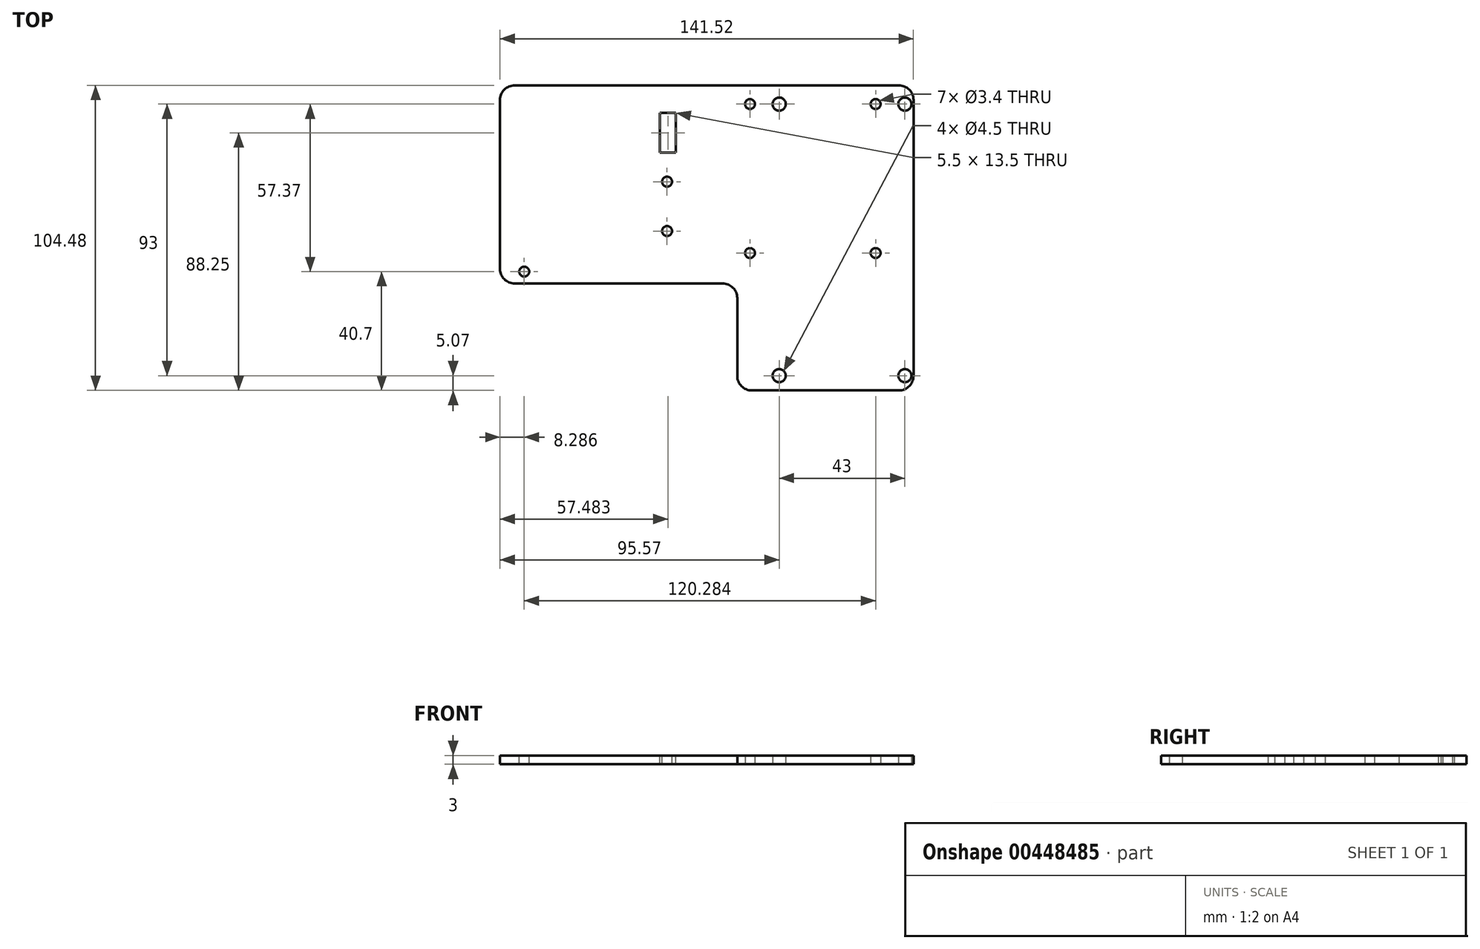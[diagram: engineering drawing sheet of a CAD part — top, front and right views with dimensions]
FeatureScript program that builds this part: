
annotation { "Feature Type Name" : "Feature", "Feature Type Description" : "" }
export const myFeature = defineFeature(function(context is Context, id is Id, definition is map)
    precondition{}
    {
        {
            var Q0;
            Q0=qCreatedBy(makeId("Top.planeOp"),FACE);
            var sketch = newSketch(context, id + "F0", { "sketchPlane" : qUnion([Q0])});
            skLineSegment(sketch, "E0.bottom", {"start": v(-21.5, 46.5) * mm, "end": v(21.5, 46.5) * mm, "construction": true});
            skLineSegment(sketch, "E0.top", {"start": v(-21.5, -46.5) * mm, "end": v(21.5, -46.5) * mm, "construction": true});
            skLineSegment(sketch, "E0.left", {"start": v(-21.5, 46.5) * mm, "end": v(-21.5, -46.5) * mm, "construction": true});
            skLineSegment(sketch, "E0.right", {"start": v(21.5, 46.5) * mm, "end": v(21.5, -46.5) * mm, "construction": true});
            skPoint(sketch, "E0.middle", {"position": v(0, 0) * mm});
            skLineSegment(sketch, "E1.bottom", {"start": v(24.45, -51.57) * mm, "end": v(-35.85, -51.57) * mm});
            skLineSegment(sketch, "E1.top", {"start": v(24.45, 52.91) * mm, "end": v(-117.07, 52.91) * mm});
            skLineSegment(sketch, "E1.left", {"start": v(24.45, -51.57) * mm, "end": v(24.45, 52.91) * mm});
            skLineSegment(sketch, "E1.right", {"start": v(-117.07, -14.94) * mm, "end": v(-117.07, 52.91) * mm});
            skPoint(sketch, "E2.orphan", {"position": v(-96.4, 75.9) * mm});
            skLineSegment(sketch, "E3.0", {"start": v(11.5, 46.5) * mm, "end": v(11.5, -4.5) * mm});
            skLineSegment(sketch, "E4.0", {"start": v(-31.5, 46.5) * mm, "end": v(-31.5, -4.5) * mm});
            skLineSegment(sketch, "E5", {"start": v(-117.07, -14.94) * mm, "end": v(-35.85, -14.94) * mm});
            skLineSegment(sketch, "E6", {"start": v(-35.85, -14.94) * mm, "end": v(-35.85, -51.57) * mm});
            skSolve(sketch);
        }
        {
            var Q0;
            Q0 = qSketchRegion(id + "F0", true);
            extrude(context, id + "F1", {"entities" : qUnion([Q0]), "depth" : 3 * mm, "offsetDistance" : 25 * mm});
        }
        {
            var Q0;
            Q0=sQuery(id+"F0.wireOp",VERTEX,"E0.left.start");
            var Q1;
            Q1=sQuery(id+"F0.wireOp",VERTEX,"E0.right.start");
            var Q2;
            Q2=sQuery(id+"F0.wireOp",VERTEX,"E0.right.end");
            var Q3;
            Q3=sQuery(id+"F0.wireOp",VERTEX,"E0.left.end");
            var Q4;
            Q4=makeQuery(id+"F1.opExtrude","SWEPT_BODY",BODY,{"disambiguationData":[OSD([sQuery(id+"F0.wireOp",EDGE,"E1.bottom"),sQuery(id+"F0.wireOp",EDGE,"E1.top"),sQuery(id+"F0.wireOp",EDGE,"E1.left"),sQuery(id+"F0.wireOp",EDGE,"E1.right"),sQuery(id+"F0.wireOp",EDGE,"YAgUvNzY-ITle-nGsT-Vmnw-g5ldA8nWUGnr"),sQuery(id+"F0.wireOp",EDGE,"XyIVaQW3-El7N-e6bz-1eAk-mJc9jGYG2OAW"),sQuery(id+"F0.wireOp",EDGE,"2inYUX5w-coaZ-2hAe-3aFK-Vs1NiTnumc5f"),sQuery(id+"F0.wireOp",EDGE,"RIFZKn75-bQRI-PPT5-OLLJ-XKhDclTj2aRo")])]});
            hole(context, id + "F2", {"style" : HoleStyle.SIMPLE, "endStyle" : HoleEndStyle.THROUGH, "oppositeDirection" : true, "holeDiameter" : 4.5 * mm, "majorDiameter" : 5 * mm, "isTappedThrough" : true, "tappedDepth" : 12 * mm, "tapClearance" : 3, "startFromSketch" : true, "locations" : qUnion([Q0, Q1, Q2, Q3]), "scope" : qUnion([Q4])});
        }
        {
            var Q0;
            Q0=makeQuery(id+"F1.opExtrude","SWEPT_EDGE",EDGE,{"disambiguationData":[OSD([sQuery(id+"F0.wireOp",EDGE,"E1.top"),sQuery(id+"F0.wireOp",EDGE,"E1.right")])]});
            var Q1;
            Q1=makeQuery(id+"F1.opExtrude","SWEPT_EDGE",EDGE,{"disambiguationData":[OSD([sQuery(id+"F0.wireOp",EDGE,"XyIVaQW3-El7N-e6bz-1eAk-mJc9jGYG2OAW"),sQuery(id+"F0.wireOp",EDGE,"2inYUX5w-coaZ-2hAe-3aFK-Vs1NiTnumc5f")])]});
            var Q2;
            Q2=makeQuery(id+"F1.opExtrude","SWEPT_EDGE",EDGE,{"disambiguationData":[OSD([sQuery(id+"F0.wireOp",EDGE,"YAgUvNzY-ITle-nGsT-Vmnw-g5ldA8nWUGnr"),sQuery(id+"F0.wireOp",EDGE,"XyIVaQW3-El7N-e6bz-1eAk-mJc9jGYG2OAW")])]});
            var Q3;
            Q3=makeQuery(id+"F1.opExtrude","SWEPT_EDGE",EDGE,{"disambiguationData":[OSD([sQuery(id+"F0.wireOp",EDGE,"YAgUvNzY-ITle-nGsT-Vmnw-g5ldA8nWUGnr"),sQuery(id+"F0.wireOp",EDGE,"RIFZKn75-bQRI-PPT5-OLLJ-XKhDclTj2aRo")])]});
            var Q4;
            Q4=makeQuery(id+"F1.opExtrude","SWEPT_EDGE",EDGE,{"disambiguationData":[OSD([sQuery(id+"F0.wireOp",EDGE,"E1.bottom"),sQuery(id+"F0.wireOp",EDGE,"2inYUX5w-coaZ-2hAe-3aFK-Vs1NiTnumc5f")])]});
            var Q5;
            Q5=makeQuery(id+"F1.opExtrude","SWEPT_EDGE",EDGE,{"disambiguationData":[OSD([sQuery(id+"F0.wireOp",EDGE,"E1.right"),sQuery(id+"F0.wireOp",EDGE,"RIFZKn75-bQRI-PPT5-OLLJ-XKhDclTj2aRo")])]});
            var Q6;
            Q6=makeQuery(id+"F1.opExtrude","SWEPT_EDGE",EDGE,{"disambiguationData":[OSD([sQuery(id+"F0.wireOp",EDGE,"E1.top"),sQuery(id+"F0.wireOp",EDGE,"E1.left")])]});
            var Q7;
            Q7=makeQuery(id+"F1.opExtrude","SWEPT_EDGE",EDGE,{"disambiguationData":[OSD([sQuery(id+"F0.wireOp",EDGE,"E1.bottom"),sQuery(id+"F0.wireOp",EDGE,"E1.left")])]});
            var Q8;
            Q8=makeQuery(id+"F1.opExtrude","SWEPT_EDGE",EDGE,{"disambiguationData":[OSD([sQuery(id+"F0.wireOp",EDGE,"Mbf7E7DW-qALH-cvkv-Damv-hvnqM2JEZsVI"),sQuery(id+"F0.wireOp",EDGE,"yL2UZmJc-QStA-b8Vo-1v86-bxjpKFNwprbL")])]});
            var Q9;
            Q9=makeQuery(id+"F1.opExtrude","SWEPT_EDGE",EDGE,{"disambiguationData":[OSD([sQuery(id+"F0.wireOp",EDGE,"qiIUHCKB-fCWY-SWhl-cjjz-M1Dty9vsqyQJ"),sQuery(id+"F0.wireOp",EDGE,"Q55u8Cbf-FWXE-ZP9w-DCtp-IPOpDFhRQxLW")])]});
            var Q10;
            Q10=makeQuery(id+"F1.opExtrude","SWEPT_EDGE",EDGE,{"disambiguationData":[OSD([sQuery(id+"F0.wireOp",EDGE,"a1f7CNFQ-nP29-92E3-ja6P-g6eo9MA6HpaG"),sQuery(id+"F0.wireOp",EDGE,"OeeX4dYa-ce1g-dk9C-RiQx-GZsGsBV5ChxM")])]});
            var Q11;
            Q11=makeQuery(id+"F1.opExtrude","SWEPT_EDGE",EDGE,{"disambiguationData":[OSD([sQuery(id+"F0.wireOp",EDGE,"OeeX4dYa-ce1g-dk9C-RiQx-GZsGsBV5ChxM"),sQuery(id+"F0.wireOp",EDGE,"j85sN3cy-DIR5-E17b-kCIM-lPXGn6SRW4FC")])]});
            var Q12;
            Q12=makeQuery(id+"F1.opExtrude","SWEPT_EDGE",EDGE,{"disambiguationData":[OSD([sQuery(id+"F0.wireOp",EDGE,"H5cnSjnK-4Nrg-yr1O-NTxU-GIKtI7yp09dG"),sQuery(id+"F0.wireOp",EDGE,"aUoxsp5O-AR9o-Et6y-4KpD-5wgRAlL37lOh")])]});
            var Q13;
            Q13=makeQuery(id+"F1.opExtrude","SWEPT_EDGE",EDGE,{"disambiguationData":[OSD([sQuery(id+"F0.wireOp",EDGE,"9UlV4Nop-iNJr-02NP-fapv-DWM8Iypxcy4n"),sQuery(id+"F0.wireOp",EDGE,"RAkMmiOb-nROR-mXBJ-D0fB-59uvw5uzIgUD")])]});
            var Q14;
            Q14=makeQuery(id+"F1.opExtrude","SWEPT_EDGE",EDGE,{"disambiguationData":[OSD([sQuery(id+"F0.wireOp",EDGE,"RpWV4TA2-qZx3-hfFS-Fjk5-bPTjN17klhtH"),sQuery(id+"F0.wireOp",EDGE,"2l11ivdO-LSoy-1MMf-z1oK-tAifx8Baqm9W")])]});
            var Q15;
            Q15=makeQuery(id+"F1.opExtrude","SWEPT_EDGE",EDGE,{"disambiguationData":[OSD([sQuery(id+"F0.wireOp",EDGE,"E5"),sQuery(id+"F0.wireOp",EDGE,"E6")])]});
            fillet(context, id + "F3", {"entities" : qUnion([Q0, Q1, Q2, Q3, Q4, Q5, Q6, Q7, Q8, Q9, Q10, Q11, Q12, Q13, Q14, Q15]), "radius" : 5 * mm, "tangentPropagation" : true, "allowEdgeOverflow" : false});
        }
        {
            var Q0;
            Q0=sQuery(id+"F0.wireOp",VERTEX,"E4.0.start");
            var Q1;
            Q1=sQuery(id+"F0.wireOp",VERTEX,"E3.0.start");
            var Q2;
            Q2=sQuery(id+"F0.wireOp",VERTEX,"E3.0.end");
            var Q3;
            Q3=sQuery(id+"F0.wireOp",VERTEX,"E4.0.end");
            var Q4;
            Q4=makeQuery(id+"F1.opExtrude","SWEPT_BODY",BODY,{"disambiguationData":[OSD([sQuery(id+"F0.wireOp",EDGE,"E1.bottom"),sQuery(id+"F0.wireOp",EDGE,"E1.top"),sQuery(id+"F0.wireOp",EDGE,"E1.left"),sQuery(id+"F0.wireOp",EDGE,"E1.right")])]});
            hole(context, id + "F4", {"style" : HoleStyle.SIMPLE, "endStyle" : HoleEndStyle.THROUGH, "oppositeDirection" : true, "standardTappedOrClearance" : lookupTablePath({ "fit" : "Normal", "standard" : "ISO", "size" : "M3", "type" : "Clearance" }), "standardBlindInLast" : lookupTablePath({ "fit" : "Normal", "standard" : "ISO", "engagement" : "75%", "pitch" : "0.5 mm", "size" : "M3", "type" : "Clearance & tapped" }), "holeDiameter" : 3.4 * mm, "majorDiameter" : 5 * mm, "isTappedThrough" : true, "tappedDepth" : 12 * mm, "tapClearance" : 3, "startFromSketch" : true, "locations" : qUnion([Q0, Q1, Q2, Q3]), "scope" : qUnion([Q4])});
        }
        {
            var Q0;
            Q0=makeQuery(id+"F1.opExtrude","CAP_FACE",FACE,{"disambiguationData":[OSD([sQuery(id+"F0.wireOp",EDGE,"E1.bottom"),sQuery(id+"F0.wireOp",EDGE,"E1.top"),sQuery(id+"F0.wireOp",EDGE,"E1.left"),sQuery(id+"F0.wireOp",EDGE,"E1.right")])],"isStart":false});
            var sketch = newSketch(context, id + "F5", { "sketchPlane" : qUnion([Q0])});
            skLineSegment(sketch, "E7", {"start": v(-62.34, 29.93) * mm, "end": v(-56.84, 29.93) * mm});
            skPoint(sketch, "E8", {"position": v(-62.34, 3.02) * mm});
            skLineSegment(sketch, "E9", {"start": v(-59.89, 43.43) * mm, "end": v(-59.89, 3.02) * mm, "construction": true});
            skPoint(sketch, "E10", {"position": v(-59.89, 19.93) * mm});
            skLineSegment(sketch, "E11", {"start": v(-59.89, 3.02) * mm, "end": v(-108.78, 3.02) * mm, "construction": true});
            skLineSegment(sketch, "E12", {"start": v(-108.78, 3.02) * mm, "end": v(-108.78, -10.87) * mm, "construction": true});
            skLineSegment(sketch, "E13", {"start": v(-56.84, 43.43) * mm, "end": v(-62.34, 43.43) * mm});
            skLineSegment(sketch, "E14", {"start": v(-62.34, 43.43) * mm, "end": v(-62.34, 29.93) * mm});
            skLineSegment(sketch, "E15", {"start": v(-56.84, 29.93) * mm, "end": v(-56.84, 43.43) * mm});
            skSolve(sketch);
        }
        {
            var Q0;
            Q0=sQuery(id+"F5.wireOp",VERTEX,"E9.end");
            var Q1;
            Q1=sQuery(id+"F5.wireOp",VERTEX,"E10");
            var Q2;
            Q2=sQuery(id+"F5.wireOp",VERTEX,"E12.end");
            var Q3;
            Q3=makeQuery(id+"F1.opExtrude","SWEPT_BODY",BODY,{"disambiguationData":[OSD([sQuery(id+"F0.wireOp",EDGE,"E1.bottom"),sQuery(id+"F0.wireOp",EDGE,"E1.top"),sQuery(id+"F0.wireOp",EDGE,"E1.left"),sQuery(id+"F0.wireOp",EDGE,"E1.right")])]});
            hole(context, id + "F6", {"style" : HoleStyle.SIMPLE, "endStyle" : HoleEndStyle.THROUGH, "standardTappedOrClearance" : lookupTablePath({ "fit" : "Normal", "standard" : "ISO", "size" : "M3", "type" : "Clearance" }), "standardBlindInLast" : lookupTablePath({ "fit" : "Normal", "standard" : "ISO", "engagement" : "75%", "pitch" : "0.5 mm", "size" : "M3", "type" : "Clearance & tapped" }), "holeDiameter" : 3.4 * mm, "majorDiameter" : 5 * mm, "isTappedThrough" : true, "tappedDepth" : 12 * mm, "tapClearance" : 3, "startFromSketch" : true, "locations" : qUnion([Q0, Q1, Q2]), "scope" : qUnion([Q3])});
        }
        {
            var Q0;
            Q0=makeQuery(id+"F5.imprint","IMPRINT",FACE,{"disambiguationData":[TD([[makeQuery(id+"F5.imprint","IMPRINT",EDGE,{"derivedFrom":sQuery(id+"F5.wireOp",EDGE,"E7")}),1.0]])]});
            extrude(context, id + "F7", {"entities" : qUnion([Q0]), "operationType" : NewBodyOperationType.REMOVE, "oppositeDirection" : true, "depth" : 25 * mm, "offsetDistance" : 25 * mm});
        }
    });
